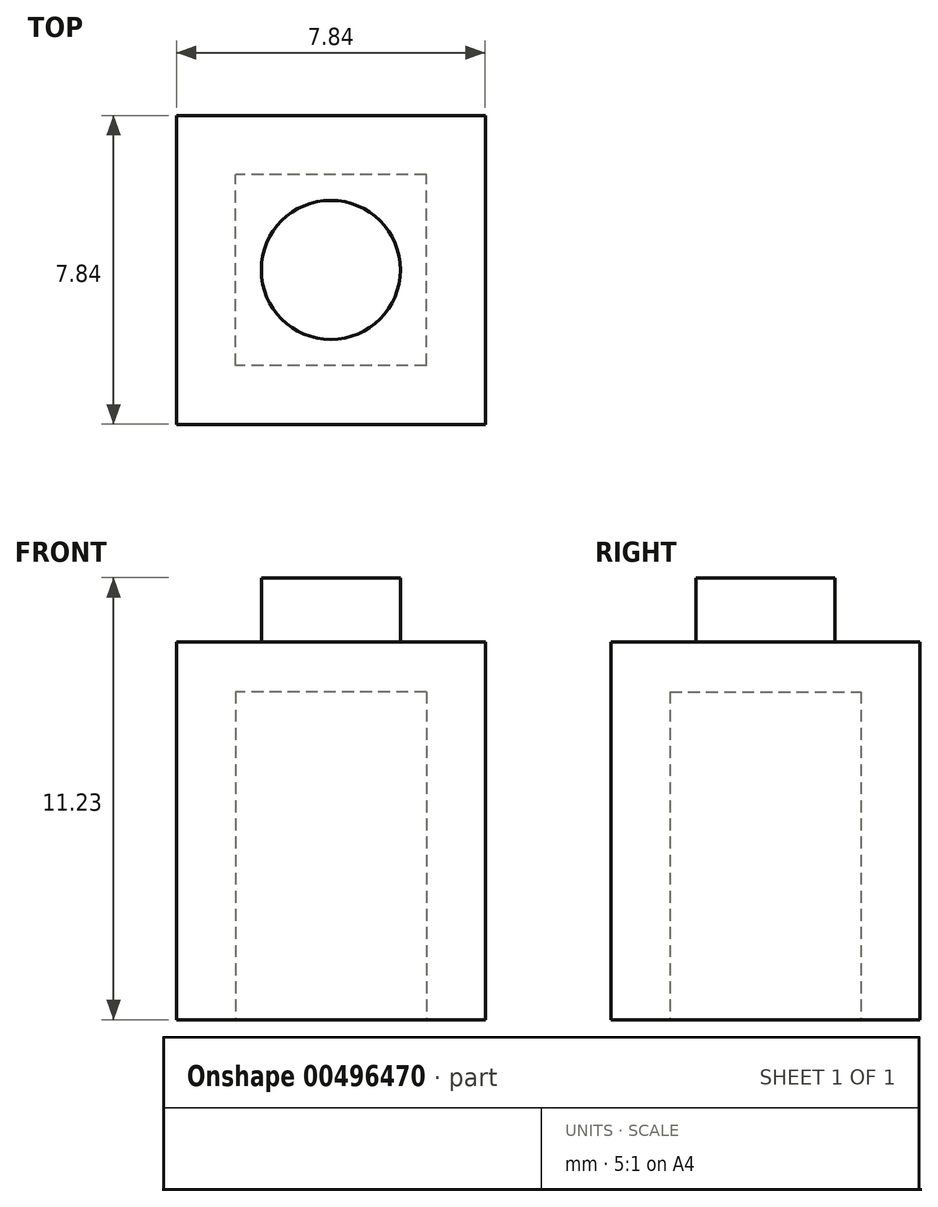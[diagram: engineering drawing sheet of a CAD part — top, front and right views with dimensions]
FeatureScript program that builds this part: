
annotation { "Feature Type Name" : "Feature", "Feature Type Description" : "" }
export const myFeature = defineFeature(function(context is Context, id is Id, definition is map)
    precondition{}
    {
        {
            var Q0;
            Q0=qCreatedBy(makeId("Top.planeOp"),FACE);
            var sketch = newSketch(context, id + "F0", { "sketchPlane" : qUnion([Q0])});
            skLineSegment(sketch, "E0.bottom", {"start": v(3.92, 3.92) * mm, "end": v(-3.92, 3.92) * mm});
            skLineSegment(sketch, "E0.top", {"start": v(3.92, -3.92) * mm, "end": v(-3.92, -3.92) * mm});
            skLineSegment(sketch, "E0.left", {"start": v(3.92, 3.92) * mm, "end": v(3.92, -3.92) * mm});
            skLineSegment(sketch, "E0.right", {"start": v(-3.92, 3.92) * mm, "end": v(-3.92, -3.92) * mm});
            skPoint(sketch, "E0.middle", {"position": v(0, 0) * mm});
            skSolve(sketch);
        }
        {
            var Q0;
            Q0=makeQuery(id+"F0.imprint","IMPRINT",FACE,{"disambiguationData":[TD([[makeQuery(id+"F0.imprint","IMPRINT",EDGE,{"derivedFrom":sQuery(id+"F0.wireOp",EDGE,"E0.bottom")}),1.0]])]});
            extrude(context, id + "F1", {"entities" : qUnion([Q0]), "depth" : 9.6 * mm});
        }
        {
            var Q0;
            Q0=makeQuery(id+"F1.opExtrude","CAP_FACE",FACE,{"disambiguationData":[OSD([sQuery(id+"F0.wireOp",EDGE,"E0.bottom"),sQuery(id+"F0.wireOp",EDGE,"E0.top"),sQuery(id+"F0.wireOp",EDGE,"E0.left"),sQuery(id+"F0.wireOp",EDGE,"E0.right")])],"isStart":false});
            var sketch = newSketch(context, id + "F2", { "sketchPlane" : qUnion([Q0])});
            skCircle(sketch, "E1", {"center": v(0, 0) * mm, "radius": 1.77 * mm});
            skSolve(sketch);
        }
        {
            var Q0;
            Q0=makeQuery(id+"F2.imprint","IMPRINT",FACE,{"disambiguationData":[TD([[makeQuery(id+"F2.imprint","IMPRINT",EDGE,{"derivedFrom":sQuery(id+"F2.wireOp",EDGE,"E1")}),1.0]])]});
            extrude(context, id + "F3", {"entities" : qUnion([Q0]), "operationType" : NewBodyOperationType.ADD, "depth" : 1.63 * mm});
        }
        {
            var Q0;
            Q0=makeQuery(id+"F1.opExtrude","CAP_FACE",FACE,{"disambiguationData":[OSD([sQuery(id+"F0.wireOp",EDGE,"E0.bottom"),sQuery(id+"F0.wireOp",EDGE,"E0.top"),sQuery(id+"F0.wireOp",EDGE,"E0.left"),sQuery(id+"F0.wireOp",EDGE,"E0.right")])],"isStart":true});
            var sketch = newSketch(context, id + "F4", { "sketchPlane" : qUnion([Q0])});
            skLineSegment(sketch, "E2.bottom", {"start": v(2.43, 2.43) * mm, "end": v(-2.43, 2.43) * mm});
            skLineSegment(sketch, "E2.top", {"start": v(2.43, -2.43) * mm, "end": v(-2.43, -2.43) * mm});
            skLineSegment(sketch, "E2.left", {"start": v(2.43, 2.43) * mm, "end": v(2.43, -2.43) * mm});
            skLineSegment(sketch, "E2.right", {"start": v(-2.43, 2.43) * mm, "end": v(-2.43, -2.43) * mm});
            skPoint(sketch, "E2.middle", {"position": v(0, 0) * mm});
            skSolve(sketch);
        }
        {
            var Q0;
            Q0=makeQuery(id+"F4.imprint","IMPRINT",FACE,{"disambiguationData":[TD([[makeQuery(id+"F4.imprint","IMPRINT",EDGE,{"derivedFrom":sQuery(id+"F4.wireOp",EDGE,"E2.bottom")}),1.0]])]});
            extrude(context, id + "F5", {"entities" : qUnion([Q0]), "operationType" : NewBodyOperationType.REMOVE, "oppositeDirection" : true, "depth" : 8.33 * mm});
        }
    });
